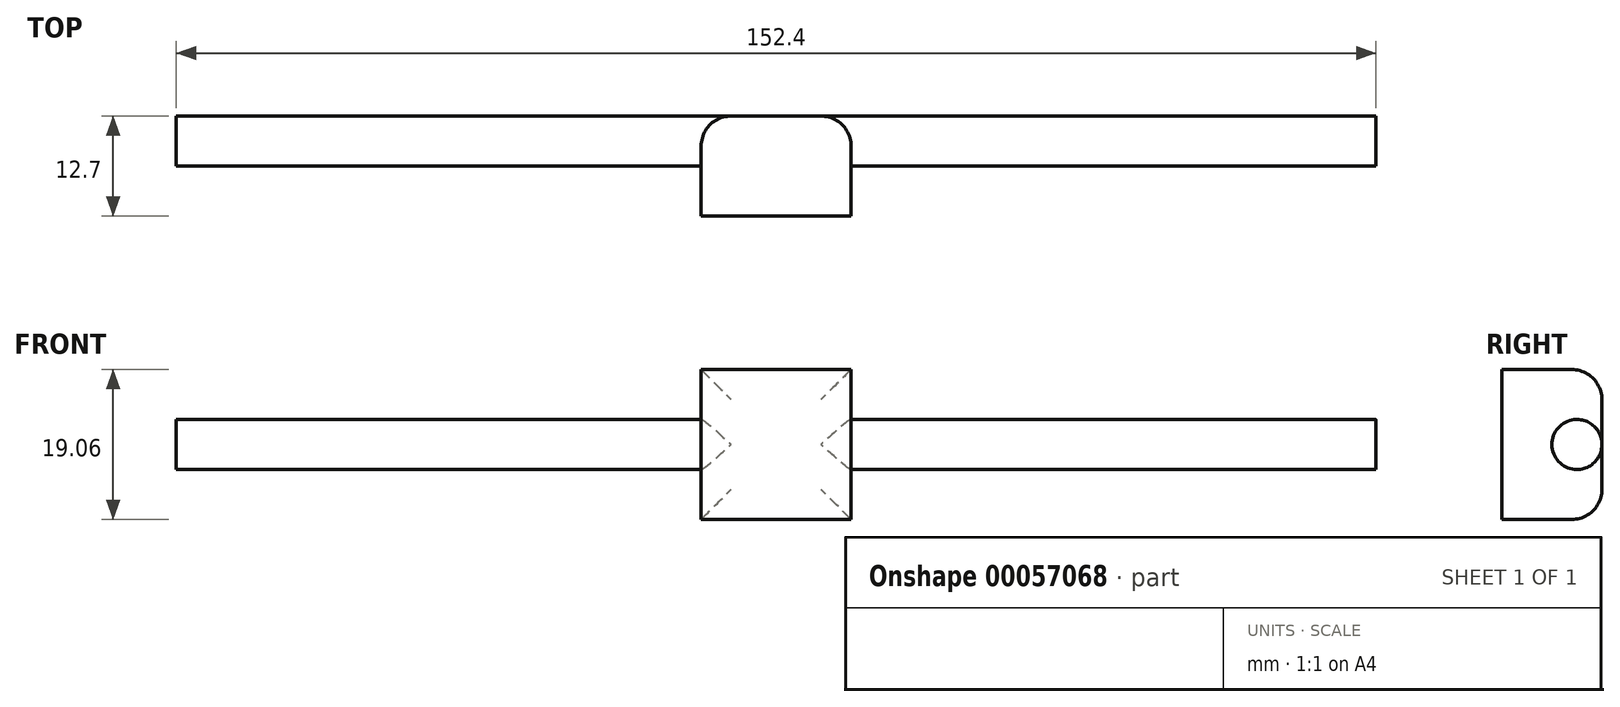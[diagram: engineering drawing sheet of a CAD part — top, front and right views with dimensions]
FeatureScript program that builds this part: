
annotation { "Feature Type Name" : "Feature", "Feature Type Description" : "" }
export const myFeature = defineFeature(function(context is Context, id is Id, definition is map)
    precondition{}
    {
        {
            var Q0;
            Q0=qCreatedBy(makeId("Front.planeOp"),FACE);
            var sketch = newSketch(context, id + "F0", { "sketchPlane" : qUnion([Q0])});
            skLineSegment(sketch, "E0.rect.bottom", {"start": v(-76.2, 3.18) * mm, "end": v(76.2, 3.18) * mm});
            skLineSegment(sketch, "E0.rect.top", {"start": v(-76.2, -3.18) * mm, "end": v(76.2, -3.18) * mm});
            skLineSegment(sketch, "E0.rect.left", {"start": v(-76.2, 3.18) * mm, "end": v(-76.2, -3.18) * mm});
            skLineSegment(sketch, "E0.rect.right", {"start": v(76.2, 3.18) * mm, "end": v(76.2, -3.18) * mm});
            skPoint(sketch, "E0.rect.middle", {"position": v(0, 0) * mm});
            skSolve(sketch);
        }
        {
            var Q0;
            Q0=makeQuery(id+"F0.imprint","IMPRINT",FACE,{"disambiguationData":[TD([[makeQuery(id+"F0.imprint","IMPRINT",EDGE,{"derivedFrom":sQuery(id+"F0.wireOp",EDGE,"E0.rect.bottom")}),-1.0]])]});
            extrude(context, id + "F1", {"entities" : qUnion([Q0]), "depth" : 6.35 * mm});
        }
        {
            var Q0;
            Q0=makeQuery(id+"F1.opExtrude","SWEPT_FACE",FACE,{"disambiguationData":[OSD([sQuery(id+"F0.wireOp",EDGE,"E0.rect.left")])]});
            var sketch = newSketch(context, id + "F2", { "sketchPlane" : qUnion([Q0])});
            skCircle(sketch, "E1", {"center": v(3.18, 0) * mm, "radius": 3.18 * mm});
            skSolve(sketch);
        }
        {
            var Q0;
            {var subQ0=sQuery(id+"F2.wireOp",EDGE,"E1");var subQ1=sQuery(id+"F0.wireOp",EDGE,"E0.rect.left");var subQ4=makeQuery(id+"F1.opExtrude","CAP_EDGE",EDGE,{"disambiguationData":[OSD([subQ1])],"isStart":true});var subQ5=makeQuery(id+"F2.imprint","INTERSECT",VERTEX,{"derivedFrom":[subQ4,subQ0]});Q0=makeQuery(id+"F2.imprint","IMPRINT",FACE,{"disambiguationData":[TD([[makeQuery(id+"F2.imprint","IMPRINT",EDGE,{"disambiguationData":[TD([[subQ5,1.0]])],"derivedFrom":subQ0}),-1.0]])]});}
            var Q1;
            {var subQ0=sQuery(id+"F2.wireOp",EDGE,"E1");var subQ1=sQuery(id+"F0.wireOp",EDGE,"E0.rect.left");var subQ4=makeQuery(id+"F1.opExtrude","CAP_EDGE",EDGE,{"disambiguationData":[OSD([subQ1])],"isStart":false});var subQ5=makeQuery(id+"F2.imprint","INTERSECT",VERTEX,{"derivedFrom":[subQ4,subQ0]});Q1=makeQuery(id+"F2.imprint","IMPRINT",FACE,{"disambiguationData":[TD([[makeQuery(id+"F2.imprint","IMPRINT",EDGE,{"disambiguationData":[TD([[subQ5,-1.0]])],"derivedFrom":subQ0}),-1.0]])]});}
            var Q2;
            {var subQ0=sQuery(id+"F2.wireOp",EDGE,"E1");var subQ1=sQuery(id+"F0.wireOp",EDGE,"E0.rect.left");var subQ2=makeQuery(id+"F1.opExtrude","CAP_EDGE",EDGE,{"disambiguationData":[OSD([subQ1])],"isStart":false});var subQ3=makeQuery(id+"F2.imprint","INTERSECT",VERTEX,{"derivedFrom":[subQ2,subQ0]});Q2=makeQuery(id+"F2.imprint","IMPRINT",FACE,{"disambiguationData":[TD([[makeQuery(id+"F2.imprint","IMPRINT",EDGE,{"disambiguationData":[TD([[subQ3,1.0]])],"derivedFrom":subQ0}),-1.0]])]});}
            var Q3;
            {var subQ0=sQuery(id+"F2.wireOp",EDGE,"E1");var subQ1=sQuery(id+"F0.wireOp",EDGE,"E0.rect.left");var subQ2=makeQuery(id+"F1.opExtrude","CAP_EDGE",EDGE,{"disambiguationData":[OSD([subQ1])],"isStart":true});var subQ3=makeQuery(id+"F2.imprint","INTERSECT",VERTEX,{"derivedFrom":[subQ2,subQ0]});Q3=makeQuery(id+"F2.imprint","IMPRINT",FACE,{"disambiguationData":[TD([[makeQuery(id+"F2.imprint","IMPRINT",EDGE,{"disambiguationData":[TD([[subQ3,-1.0]])],"derivedFrom":subQ0}),-1.0]])]});}
            extrude(context, id + "F3", {"entities" : qUnion([Q0, Q1, Q2, Q3]), "operationType" : NewBodyOperationType.REMOVE, "oppositeDirection" : true, "depth" : 203.2 * mm});
        }
        {
            var Q0;
            Q0=qCreatedBy(makeId("Front.planeOp"),FACE);
            var sketch = newSketch(context, id + "F4", { "sketchPlane" : qUnion([Q0])});
            skLineSegment(sketch, "E2.rect.bottom", {"start": v(9.53, 9.53) * mm, "end": v(-9.53, 9.53) * mm});
            skLineSegment(sketch, "E2.rect.top", {"start": v(9.53, -9.53) * mm, "end": v(-9.53, -9.53) * mm});
            skLineSegment(sketch, "E2.rect.left", {"start": v(9.53, 9.53) * mm, "end": v(9.53, -9.52) * mm});
            skLineSegment(sketch, "E2.rect.right", {"start": v(-9.53, 9.53) * mm, "end": v(-9.53, -9.53) * mm});
            skPoint(sketch, "E2.rect.middle", {"position": v(0, 0) * mm});
            skSolve(sketch);
        }
        {
            var Q0;
            Q0=makeQuery(id+"F4.imprint","IMPRINT",FACE,{"disambiguationData":[TD([[makeQuery(id+"F4.imprint","IMPRINT",EDGE,{"derivedFrom":sQuery(id+"F4.wireOp",EDGE,"E2.rect.bottom")}),1.0]])]});
            extrude(context, id + "F5", {"entities" : qUnion([Q0]), "operationType" : NewBodyOperationType.ADD, "depth" : 12.7 * mm});
        }
        {
            var Q0;
            Q0=makeQuery(id+"F5.opExtrude","CAP_EDGE",EDGE,{"disambiguationData":[OSD([sQuery(id+"F4.wireOp",EDGE,"E2.rect.top")])],"isStart":true});
            var Q1;
            {var subQ6=sQuery(id+"F4.wireOp",EDGE,"E2.rect.left");var subQ7=sQuery(id+"F4.wireOp",EDGE,"E2.rect.top");Q1=makeQuery(id+"F5.boolean.opBoolean","SPLIT",EDGE,{"disambiguationData":[TD([makeQuery(id+"F5.opExtrude","SWEPT_FACE",FACE,{"disambiguationData":[OSD([subQ7])]})])],"derivedFrom":makeQuery(id+"F5.opExtrude","CAP_EDGE",EDGE,{"disambiguationData":[OSD([subQ6])],"isStart":true})});}
            var Q2;
            Q2=makeQuery(id+"F5.opExtrude","CAP_EDGE",EDGE,{"disambiguationData":[OSD([sQuery(id+"F4.wireOp",EDGE,"E2.rect.bottom")])],"isStart":true});
            var Q3;
            {var subQ6=sQuery(id+"F4.wireOp",EDGE,"E2.rect.right");var subQ7=sQuery(id+"F4.wireOp",EDGE,"E2.rect.top");Q3=makeQuery(id+"F5.boolean.opBoolean","SPLIT",EDGE,{"disambiguationData":[TD([makeQuery(id+"F5.opExtrude","SWEPT_FACE",FACE,{"disambiguationData":[OSD([subQ7])]})])],"derivedFrom":makeQuery(id+"F5.opExtrude","CAP_EDGE",EDGE,{"disambiguationData":[OSD([subQ6])],"isStart":true})});}
            fillet(context, id + "F6", {"entities" : qUnion([Q0, Q1, Q2, Q3]), "radius" : 3.8 * mm, "tangentPropagation" : true, "allowEdgeOverflow" : false});
        }
    });
